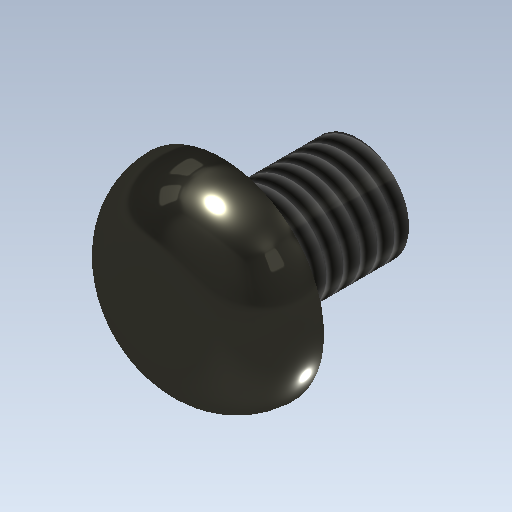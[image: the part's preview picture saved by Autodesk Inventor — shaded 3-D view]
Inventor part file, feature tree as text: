
AUTODESK INVENTOR PART (.ipt)
format: ipt  version: 2020.2 (Build 242310000, 310)  size: 167,424 bytes
history: native  units: mm
features: extrude x2, sketch x2, other x1, fillet x1, thread x1
ambient origin geometry x1: Origin
bodies: Body1 (feature_tree)
feature tree (7):
  other  "ソリッド1"
  extrude  "押し出し1"  Depth=3.0mm
  extrude  "押し出し2"  Depth=4.0mm TaperAngle=0.0deg
  fillet  "フィレット1"  Radius=6.0mm
  thread  "ねじ1"
  sketch  "スケッチ1"
  sketch  "スケッチ2"
